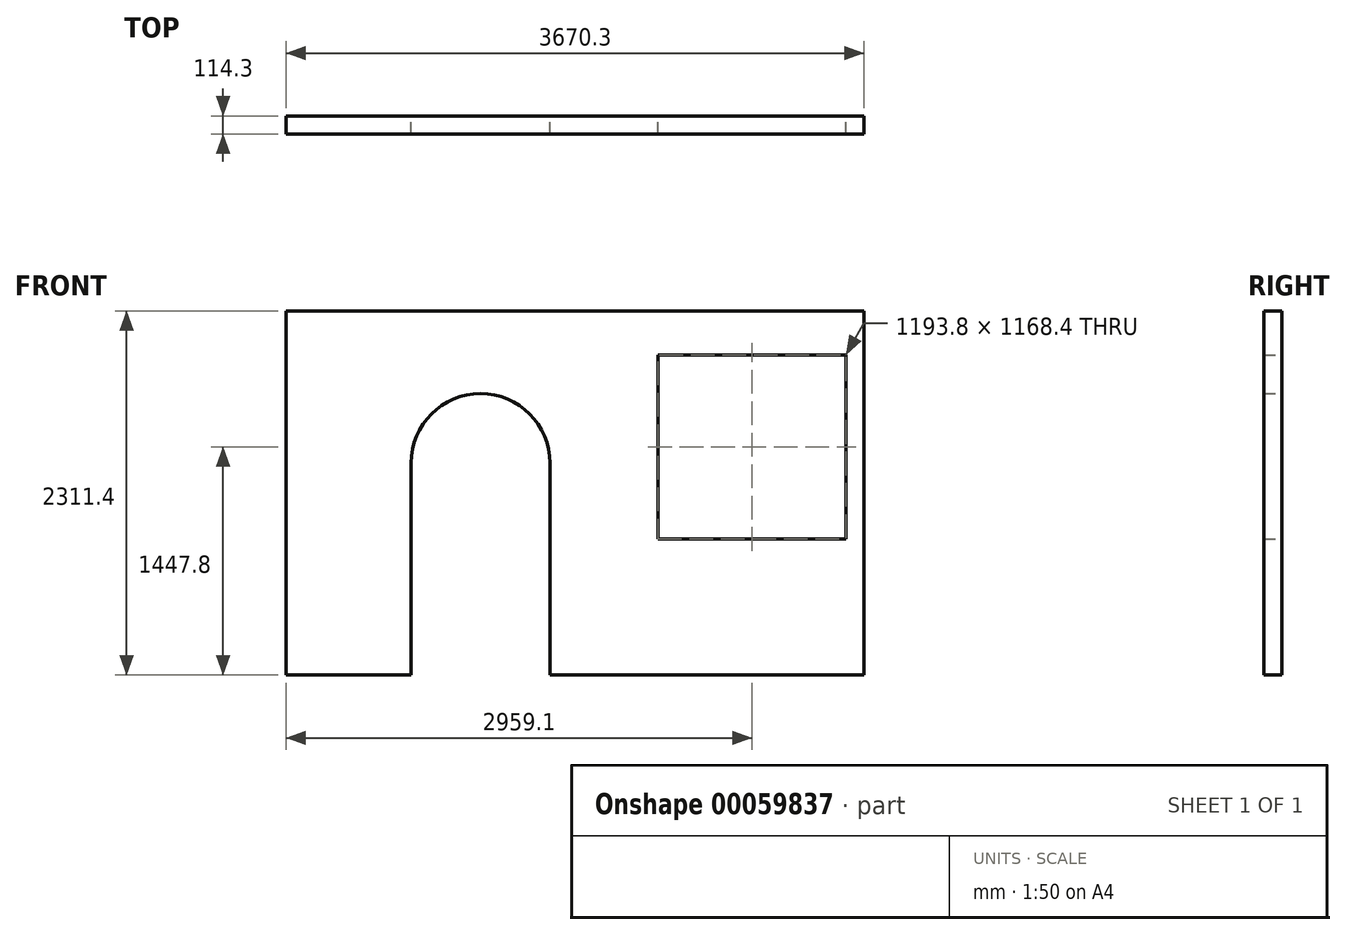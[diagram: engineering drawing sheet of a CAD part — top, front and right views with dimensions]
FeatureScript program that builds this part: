
annotation { "Feature Type Name" : "Feature", "Feature Type Description" : "" }
export const myFeature = defineFeature(function(context is Context, id is Id, definition is map)
    precondition{}
    {
        {
            var Q0;
            Q0=qCreatedBy(makeId("Front.planeOp"),FACE);
            var sketch = newSketch(context, id + "F0", { "sketchPlane" : qUnion([Q0])});
            skLineSegment(sketch, "E0.bottom", {"start": v(-1850.24, 2277.8) * mm, "end": v(1820.06, 2277.8) * mm});
            skLineSegment(sketch, "E0.top", {"start": v(-1850.24, -33.6) * mm, "end": v(-1056.5, -33.6) * mm});
            skLineSegment(sketch, "E0.left", {"start": v(-1850.24, 2277.8) * mm, "end": v(-1850.24, -33.6) * mm});
            skLineSegment(sketch, "E0.right", {"start": v(1820.06, 2277.8) * mm, "end": v(1820.06, -33.6) * mm});
            skLineSegment(sketch, "E1.bottom", {"start": v(511.96, 1998.4) * mm, "end": v(1705.76, 1998.4) * mm});
            skLineSegment(sketch, "E1.top", {"start": v(511.96, 830) * mm, "end": v(1705.76, 830) * mm});
            skLineSegment(sketch, "E1.left", {"start": v(511.96, 1998.4) * mm, "end": v(511.96, 830) * mm});
            skLineSegment(sketch, "E1.right", {"start": v(1705.76, 1998.4) * mm, "end": v(1705.76, 830) * mm});
            skLineSegment(sketch, "E2.left", {"start": v(-1056.5, 1312.6) * mm, "end": v(-1056.5, -33.6) * mm});
            skLineSegment(sketch, "E2.right", {"start": v(-173.84, 1312.6) * mm, "end": v(-173.84, -33.6) * mm});
            skArc(sketch, "E3", {"start": v(-173.84, 1312.6) * mm, "mid": v(-615.17, 1753.93) * mm, "end": v(-1056.5, 1312.6) * mm});
            skLineSegment(sketch, "E4.trimOffspring", {"start": v(-173.84, -33.6) * mm, "end": v(1820.06, -33.6) * mm});
            skSolve(sketch);
        }
        {
            var Q0;
            Q0=makeQuery(id+"F0.imprint","IMPRINT",FACE,{"disambiguationData":[TD([[makeQuery(id+"F0.imprint","IMPRINT",EDGE,{"derivedFrom":sQuery(id+"F0.wireOp",EDGE,"E0.bottom")}),-1.0]])]});
            extrude(context, id + "F1", {"entities" : qUnion([Q0]), "depth" : 114.3 * mm});
        }
    });
